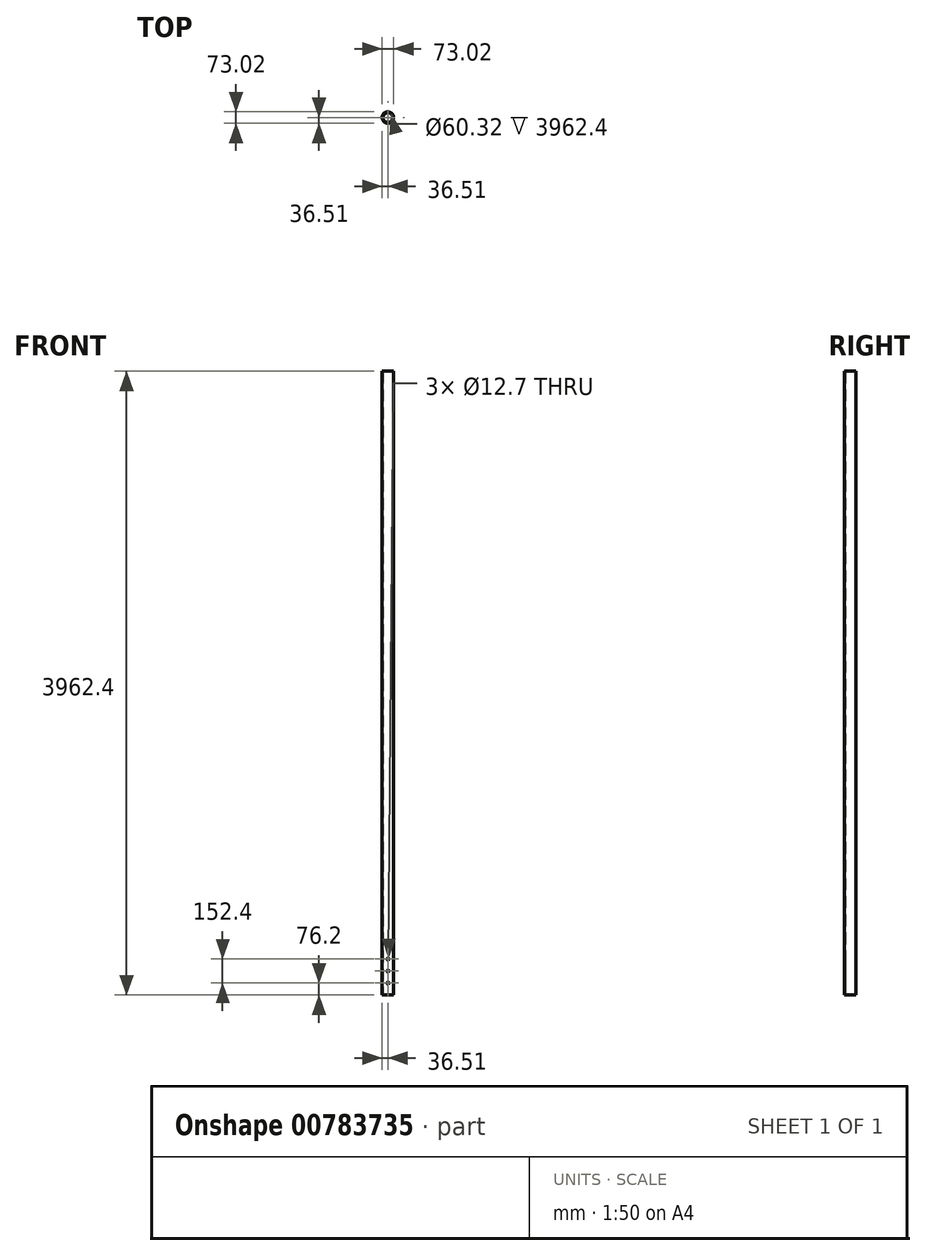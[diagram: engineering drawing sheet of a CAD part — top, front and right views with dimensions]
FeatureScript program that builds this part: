
annotation { "Feature Type Name" : "Feature", "Feature Type Description" : "" }
export const myFeature = defineFeature(function(context is Context, id is Id, definition is map)
    precondition{}
    {
        {
            var Q0;
            Q0=qCreatedBy(makeId("Top.planeOp"),FACE);
            var sketch = newSketch(context, id + "F0", { "sketchPlane" : qUnion([Q0])});
            skCircle(sketch, "E0", {"center": v(0, 0) * mm, "radius": 30.16 * mm});
            skCircle(sketch, "E1", {"center": v(0, 0) * mm, "radius": 36.51 * mm});
            skSolve(sketch);
        }
        {
            var Q0;
            Q0=makeQuery(id+"F0.imprint","IMPRINT",FACE,{"disambiguationData":[TD([[makeQuery(id+"F0.imprint","IMPRINT",EDGE,{"derivedFrom":sQuery(id+"F0.wireOp",EDGE,"E0")}),-1.0]])]});
            extrude(context, id + "F1", {"entities" : qUnion([Q0]), "depth" : 3962.4 * mm, "offsetDistance" : 25.4 * mm});
        }
        {
            var Q0;
            Q0=qCreatedBy(makeId("Top.planeOp"),FACE);
            var sketch = newSketch(context, id + "F2", { "sketchPlane" : qUnion([Q0])});
            skLineSegment(sketch, "E2.bottom", {"start": v(-36.5, 0) * mm, "end": v(36.53, 0) * mm});
            skLineSegment(sketch, "E2.top", {"start": v(-36.5, -36.53) * mm, "end": v(36.53, -36.53) * mm});
            skLineSegment(sketch, "E2.left", {"start": v(-36.5, 0) * mm, "end": v(-36.5, -36.53) * mm});
            skLineSegment(sketch, "E2.right", {"start": v(36.53, 0) * mm, "end": v(36.53, -36.53) * mm});
            skSolve(sketch);
        }
        {
            var Q0;
            Q0=sQuery(id+"F2.wireOp",EDGE,"E2.bottom");
            cPlane(context, id + "F3", {"entities" : qUnion([Q0]), "cplaneType" : CPlaneType.LINE_ANGLE, "offset" : 25.4 * mm, "angle" : 0 * degree, "width" : 152.4 * mm, "height" : 152.4 * mm});
        }
        {
            var Q0;
            Q0=qCreatedBy(id+"F3.planeOp",FACE);
            var sketch = newSketch(context, id + "F4", { "sketchPlane" : qUnion([Q0])});
            skCircle(sketch, "E3", {"center": v(0, 76.2) * mm, "radius": 6.35 * mm});
            skCircle(sketch, "E4", {"center": v(0, 152.4) * mm, "radius": 6.35 * mm});
            skCircle(sketch, "E5", {"center": v(0, 228.6) * mm, "radius": 6.35 * mm});
            skSolve(sketch);
        }
        {
            var Q0;
            Q0 = qSketchRegion(id + "F4", true);
            var Q1;
            Q1=makeQuery(id+"F1.opExtrude","SWEPT_FACE",FACE,{"disambiguationData":[OSD([sQuery(id+"F0.wireOp",EDGE,"E1")])]});
            extrude(context, id + "F5", {"entities" : qUnion([Q0]), "operationType" : NewBodyOperationType.REMOVE, "endBound" : BoundingType.UP_TO_SURFACE, "oppositeDirection" : true, "depth" : 25.4 * mm, "endBoundEntityFace" : qUnion([Q1]), "offsetDistance" : 25.4 * mm});
        }
    });
